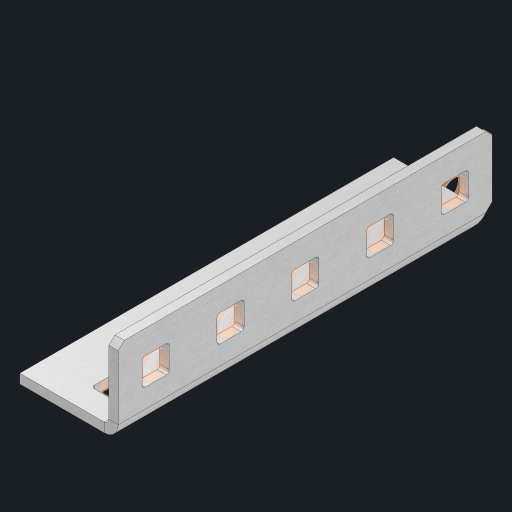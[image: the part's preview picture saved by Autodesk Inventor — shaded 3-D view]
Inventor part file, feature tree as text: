
AUTODESK INVENTOR PART (.ipt)
format: ipt  version: 2023 (Build 270158000, 158)  size: 498,176 bytes
history: native  units: in
note: dims shown in document units (in); Inventor stores cm internally (conversion verified against a paired STEP export)
features: other x15, sheet_metal_op x10, extrude x9, sketch x8, mirror x1, pattern_linear x1, chamfer x1
ambient origin geometry x8: Origin, YZ Plane, XZ Plane, XY Plane, X Axis, Y Axis, Z Axis, Center Point
bodies: Solid1 (feature_tree), Body (feature_tree)
feature tree (45):
  other  "Flange Pattern Plane"
  sheet_metal_op  "Flange Pattern"
  sheet_metal_op  "Body Pattern"
  other  "Arc Length"
  mirror  "Notch Mirror"
  pattern_linear  "Notch Pattern"  Spacing1=0.25in  [1 undecoded]
  chamfer  "End Chamfer"
  extrude  "Half Cut"  Depth=0.0625in
  sketch  "Sketch1"  dims[d0=1.5in]
  other  "Plate1"
  sketch  "Sketch2"  dims[d1=2.5in]
  other  "Plate2"
  sheet_metal_op  "Bend1"
  sheet_metal_op  "Corner1"
  sketch  "Sketch3"  dims[d2=0.0625in]
  other  "Flange Pattern Sketch"
  sketch  "Sketch7"  dims[d3=0.0625in]
  other  "Srf1"
  other  "Srf2"
  sketch  "Sketch8"  dims[d4=0.0312in]
  sketch  "Sketch9"  dims[d5=0.125in]
  other  "Srf91"
  sheet_metal_op  "Body Pattern Sketch"
  other  "Srf92"
  sketch  "Sketch13"  dims[d6=0.0625in]
  sketch  "Sketch14"  dims[d7=0.5in d8=90.0deg d9=0.0312in d10=0.25in d11=0.0625in d12=0.0625in d16=0.182in d17=0.02in d18=0.0625in d19=0.0in d20=0.25in d21=0.25in d46=0.172in d47=1.0in d48=0.0in d49=0.182in d50=0.02in d51=0.25in d52=0.25in d53=0.0625in d54=0.0in d55=0.172in d56=1.0in d57=0.0in d60=1.9685in d62=0.5in d63=0.3937in d65=0.5in d85=0.1473in d86=0.1782in d88=0.04in d89=0.0625in d90=0.0in d91=0.04in d92=0.0491in d95=2.5in d96=0.04in d97=0.25in d98=45.0deg d101=0.0in d102=2.497in d131=0.5in d132=1.9685in d134=0.5in d139=0.5in]
  other  "Srf856"
  other  "Srf1310"
  other  "Srf1311"
  other  "Srf1312"
  other  "Srf1376"
  other  "Srf1377"
  sheet_metal_op  "Flange Stamp"
  sheet_metal_op  "Flange Circle"
  sheet_metal_op  "Body Stamp"
  sheet_metal_op  "Body Circle"
  sheet_metal_op  "Notch"
  extrude  "ExtrusionSrf2"  Depth=0.0625in
  extrude  "ExtrusionSrf92"  Depth=0.5in
  extrude  "ExtrusionSrf856"  Depth=0.02in
  extrude  "ExtrusionSrf1310"  Depth=0.0625in
  extrude  "ExtrusionSrf1311"  TaperAngle=0.0deg  [1 undecoded]
  extrude  "ExtrusionSrf1312"  Depth=0.5in
  extrude  "ExtrusionSrf1376"  Depth=0.5in
  extrude  "ExtrusionSrf1377"  Depth=0.5in
note: 2 required parameter values undecoded (feature->parameter linkage not recoverable at this tier; creation-order binding heuristic only, values carry confidence <= 0.55)
